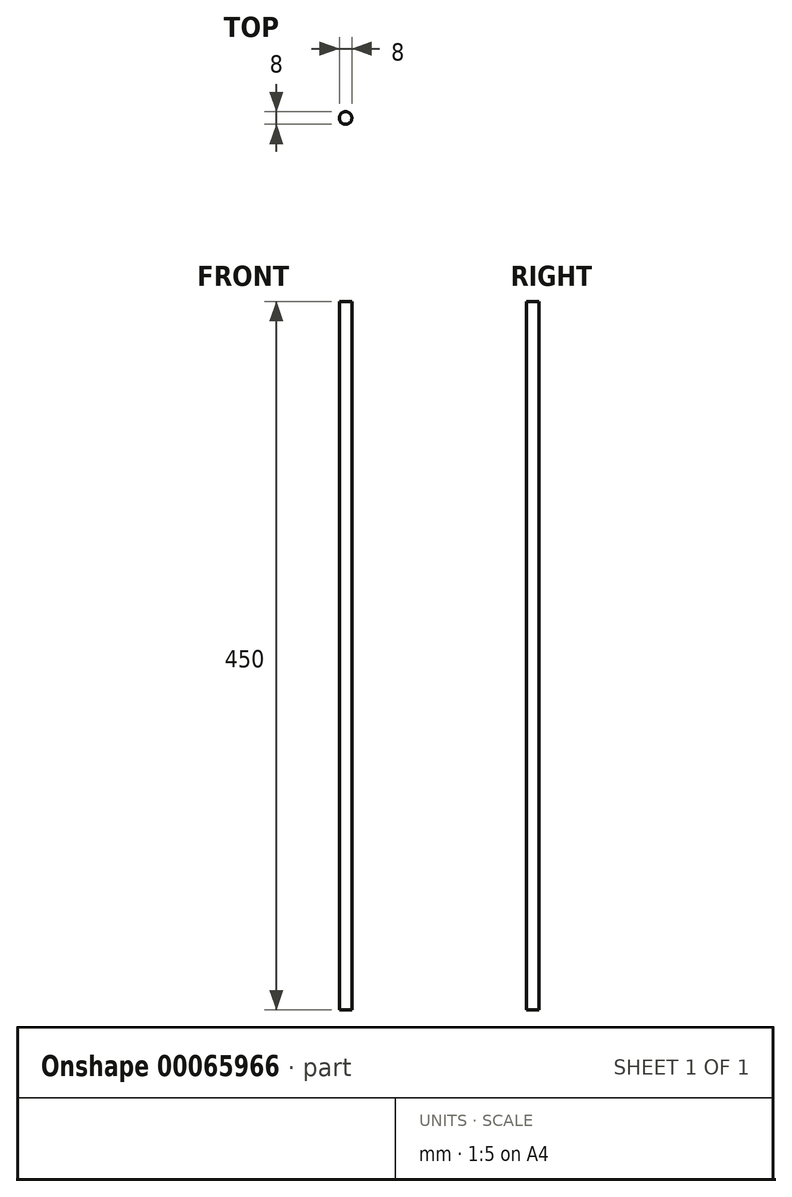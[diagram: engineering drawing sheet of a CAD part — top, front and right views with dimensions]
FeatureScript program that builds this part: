
annotation { "Feature Type Name" : "Feature", "Feature Type Description" : "" }
export const myFeature = defineFeature(function(context is Context, id is Id, definition is map)
    precondition{}
    {
        {
            var Q0;
            Q0=qCreatedBy(makeId("Top.planeOp"),FACE);
            var sketch = newSketch(context, id + "F0", { "sketchPlane" : qUnion([Q0])});
            skCircle(sketch, "E0", {"center": v(0, 0) * mm, "radius": 4 * mm});
            skSolve(sketch);
        }
        {
            var Q0;
            Q0=makeQuery(id+"F0.imprint","IMPRINT",FACE,{"disambiguationData":[TD([[makeQuery(id+"F0.imprint","IMPRINT",EDGE,{"derivedFrom":sQuery(id+"F0.wireOp",EDGE,"E0")}),1.0]])]});
            extrude(context, id + "F1", {"entities" : qUnion([Q0]), "depth" : 450 * mm});
        }
    });
